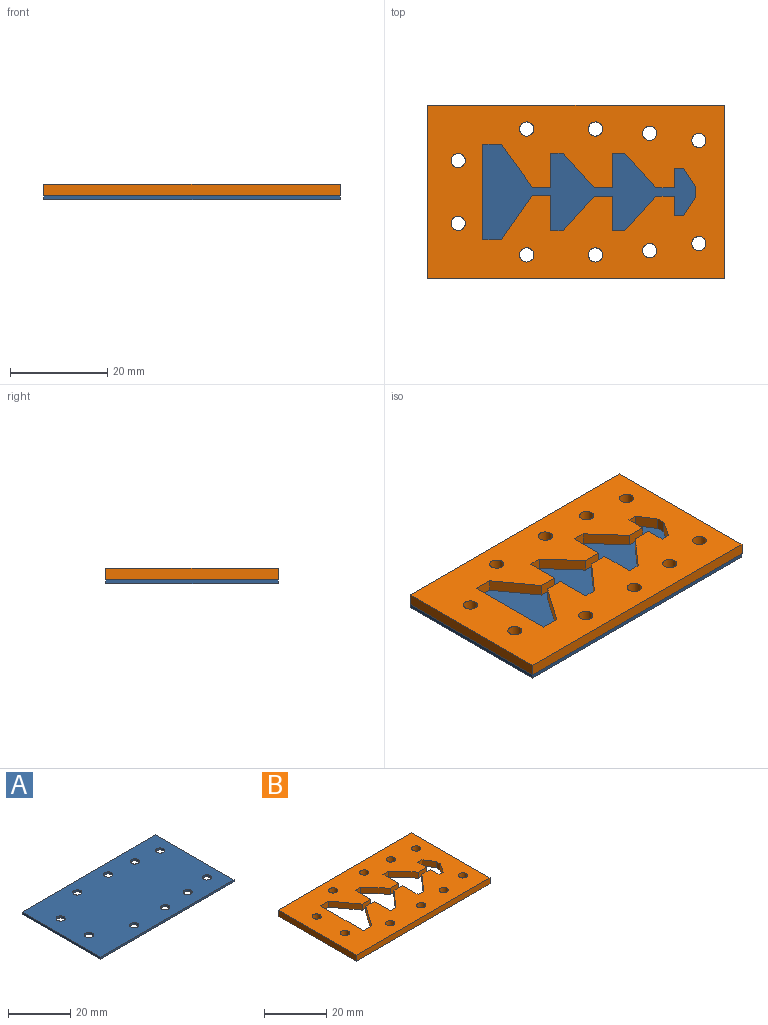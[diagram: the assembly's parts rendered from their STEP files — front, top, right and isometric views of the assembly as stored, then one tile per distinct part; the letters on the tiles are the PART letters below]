
ASSEMBLY  parts=2 mates=1
PART A: 16 faces, bbox 61x35.6x0.8 mm
  f0: plane 35.56x0.79mm, normal (-1,0,0), area 28.2mm2, adj f1,f13,f14,f15
  f1: plane 60.96x0.79mm, normal (0,-1,0), area 48.4mm2, adj f0,f2,f14,f15
  f2: plane 35.56x0.79mm, normal (1,0,0), area 28.2mm2, adj f1,f13,f14,f15
  f3: cylinder r=1.46mm len=2.92mm, axis (0,0,-1), area 7.3mm2, adj f14,f15
  f4: cylinder r=1.46mm len=2.92mm, axis (0,0,-1), area 7.3mm2, adj f14,f15
  f5: cylinder r=1.46mm len=2.92mm, axis (0,0,-1), area 7.3mm2, adj f14,f15
  f6: cylinder r=1.46mm len=2.92mm, axis (0,0,-1), area 7.3mm2, adj f14,f15
  f7: cylinder r=1.46mm len=2.92mm, axis (0,0,-1), area 7.3mm2, adj f14,f15
  f8: cylinder r=1.46mm len=2.92mm, axis (0,0,-1), area 7.3mm2, adj f14,f15
  f9: cylinder r=1.46mm len=2.92mm, axis (0,0,-1), area 7.3mm2, adj f14,f15
  f10: cylinder r=1.46mm len=2.92mm, axis (0,0,-1), area 7.3mm2, adj f14,f15
  f11: cylinder r=1.46mm len=2.92mm, axis (0,0,-1), area 7.3mm2, adj f14,f15
  f12: cylinder r=1.46mm len=2.92mm, axis (0,0,-1), area 7.3mm2, adj f14,f15
  f13: plane 60.96x0.79mm, normal (0,1,0), area 48.4mm2, adj f0,f2,f14,f15
  f14: plane 60.96x35.56mm, normal (0,0,1), area 2100.7mm2, adj f0,f1,f2,f3,f4,f5,f6,f7
  f15: plane 60.96x35.56mm, normal (0,0,-1), area 2100.7mm2, adj f0,f1,f2,f3,f4,f5,f6,f7
PART B: 46 faces, bbox 61x35.6x2.4 mm
  f0: plane 8.79x6.35mm, normal (-0.81,-0.59,0), area 25.8mm2, adj f1,f43,f44,f45
  f1: plane 3.81x2.38mm, normal (0,-1,0), area 9.1mm2, adj f0,f2,f44,f45
  f2: plane 7.01x2.38mm, normal (1,0,0), area 16.7mm2, adj f1,f3,f44,f45
  f3: plane 2.54x2.38mm, normal (0,-1,0), area 6mm2, adj f2,f4,f44,f45
  f4: plane 7.14x6.35mm, normal (-0.75,-0.66,0), area 22.7mm2, adj f3,f5,f44,f45
  f5: plane 3.81x2.38mm, normal (0,-1,0), area 9.1mm2, adj f4,f6,f44,f45
  f6: plane 7.14x2.38mm, normal (1,0,0), area 17mm2, adj f5,f7,f44,f45
  f7: plane 2.54x2.38mm, normal (0,-1,0), area 6mm2, adj f6,f8,f44,f45
  f8: plane 7.14x6.35mm, normal (-0.75,-0.66,0), area 22.7mm2, adj f7,f9,f44,f45
  f9: plane 3.81x2.38mm, normal (0,-1,0), area 9.1mm2, adj f8,f10,f44,f45
  f10: plane 3.96x2.38mm, normal (1,0,0), area 9.4mm2, adj f9,f11,f44,f45
  f11: plane 2.38x1.91mm, normal (0,-1,0), area 4.5mm2, adj f10,f12,f44,f45
  f12: plane 3.98x2.54mm, normal (-0.84,-0.54,0), area 11.2mm2, adj f11,f13,f44,f45
  f13: plane 2.38x1.69mm, normal (-1,0,0), area 4mm2, adj f12,f14,f44,f45
  f14: plane 3.98x2.54mm, normal (-0.84,0.54,0), area 11.2mm2, adj f13,f15,f44,f45
  f15: plane 2.38x1.91mm, normal (0,1,0), area 4.5mm2, adj f14,f16,f44,f45
  f16: plane 4x2.38mm, normal (1,0,0), area 9.5mm2, adj f15,f17,f44,f45
  f17: plane 3.81x2.38mm, normal (0,1,0), area 9.1mm2, adj f16,f18,f44,f45
  f18: plane 7.17x6.35mm, normal (-0.75,0.66,0), area 22.8mm2, adj f17,f19,f44,f45
  f19: plane 2.54x2.38mm, normal (0,1,0), area 6mm2, adj f18,f20,f44,f45
  f20: plane 7.17x2.38mm, normal (1,0,0), area 17.1mm2, adj f19,f21,f44,f45
  f21: plane 3.81x2.38mm, normal (0,1,0), area 9.1mm2, adj f20,f22,f44,f45
  f22: plane 7.17x6.35mm, normal (-0.75,0.66,0), area 22.8mm2, adj f21,f23,f44,f45
  f23: plane 2.54x2.38mm, normal (0,1,0), area 6mm2, adj f22,f24,f44,f45
  f24: plane 7.3x2.38mm, normal (1,0,0), area 17.4mm2, adj f23,f25,f44,f45
  f25: plane 3.81x2.38mm, normal (0,1,0), area 9.1mm2, adj f24,f26,f44,f45
  f26: plane 9.08x6.35mm, normal (-0.82,0.57,0), area 26.4mm2, adj f25,f27,f44,f45
  f27: plane 3.81x2.38mm, normal (0,1,0), area 9.1mm2, adj f26,f28,f44,f45
  f28: plane 19.56x2.38mm, normal (1,0,0), area 46.6mm2, adj f27,f43,f44,f45
  f29: plane 60.96x2.38mm, normal (0,1,0), area 145.2mm2, adj f30,f42,f44,f45
  f30: plane 35.56x2.38mm, normal (-1,0,0), area 84.7mm2, adj f29,f31,f44,f45
  f31: plane 60.96x2.38mm, normal (0,-1,0), area 145.2mm2, adj f30,f42,f44,f45
  f32: cylinder r=1.46mm len=2.92mm, axis (0,0,1), area 21.9mm2, adj f44,f45
  f33: cylinder r=1.46mm len=2.92mm, axis (0,0,1), area 21.9mm2, adj f44,f45
  f34: cylinder r=1.46mm len=2.92mm, axis (0,0,1), area 21.9mm2, adj f44,f45
  f35: cylinder r=1.46mm len=2.92mm, axis (0,0,1), area 21.9mm2, adj f44,f45
  f36: cylinder r=1.46mm len=2.92mm, axis (0,0,1), area 21.9mm2, adj f44,f45
  f37: cylinder r=1.46mm len=2.92mm, axis (0,0,1), area 21.9mm2, adj f44,f45
  f38: cylinder r=1.46mm len=2.92mm, axis (0,0,1), area 21.9mm2, adj f44,f45
  f39: cylinder r=1.46mm len=2.92mm, axis (0,0,1), area 21.9mm2, adj f44,f45
  f40: cylinder r=1.46mm len=2.92mm, axis (0,0,1), area 21.9mm2, adj f44,f45
  f41: cylinder r=1.46mm len=2.92mm, axis (0,0,1), area 21.9mm2, adj f44,f45
  f42: plane 35.56x2.38mm, normal (1,0,0), area 84.7mm2, adj f29,f31,f44,f45
  f43: plane 3.81x2.38mm, normal (0,-1,0), area 9.1mm2, adj f0,f28,f44,f45
  f44: plane 60.96x35.56mm, normal (0,0,-1), area 1712.9mm2, adj f0,f1,f2,f3,f4,f5,f6,f7
  f45: plane 60.96x35.56mm, normal (0,0,1), area 1712.9mm2, adj f0,f1,f2,f3,f4,f5,f6,f7
PLACE A t=(14.66,-16.49,8.32)mm
PLACE B t=(5.66,-0.26,11.49)mm
MATE fastened A.f14 <-> B.f44  axis (0,0,1) through (-34.84,-13.43,9.11)mm
